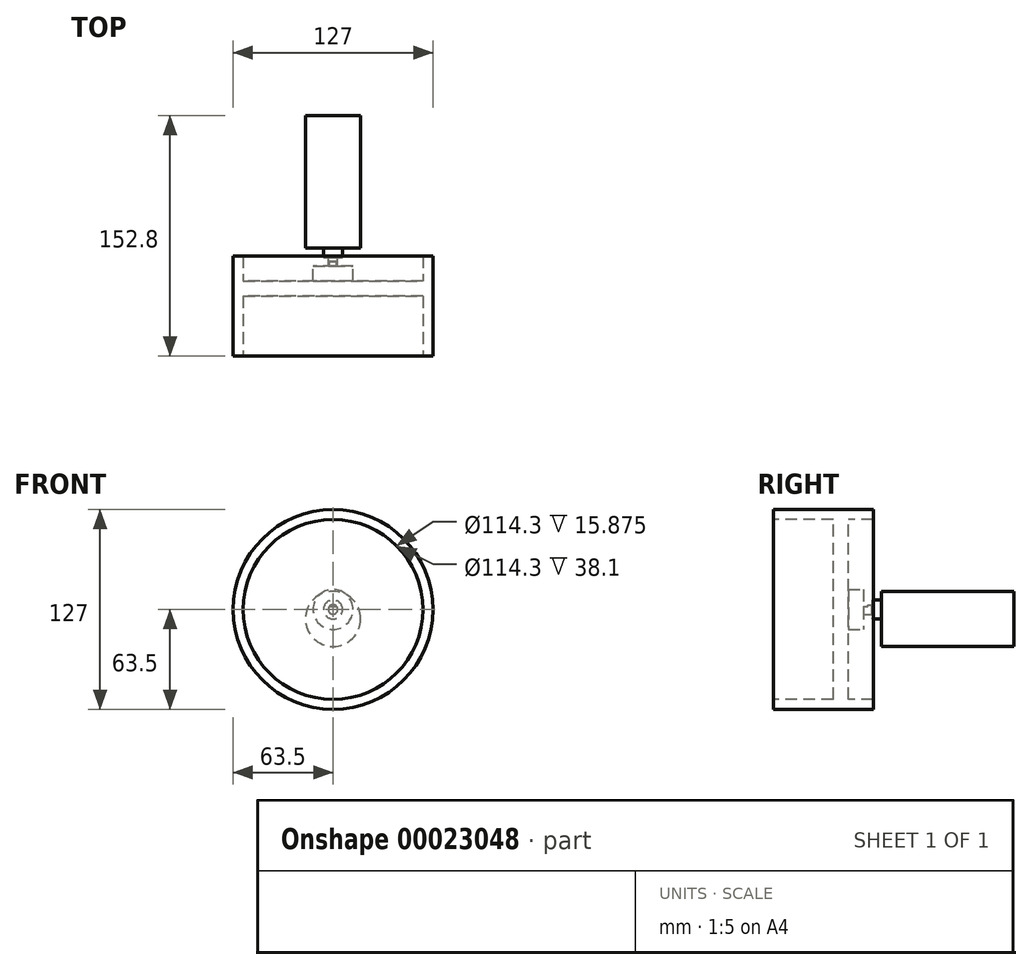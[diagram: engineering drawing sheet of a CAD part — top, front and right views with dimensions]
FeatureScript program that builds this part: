
annotation { "Feature Type Name" : "Feature", "Feature Type Description" : "" }
export const myFeature = defineFeature(function(context is Context, id is Id, definition is map)
    precondition{}
    {
        {
            var Q0;
            Q0=qCreatedBy(makeId("Front.planeOp"),FACE);
            var sketch = newSketch(context, id + "F0", { "sketchPlane" : qUnion([Q0])});
            skArc(sketch, "E0", {"start": v(-2.24, 2) * mm, "mid": v(0, -3) * mm, "end": v(2.24, 2) * mm});
            skPoint(sketch, "E1.start.orphan", {"position": v(0, -3) * mm});
            skPoint(sketch, "E2", {"position": v(-2.24, 2) * mm});
            skPoint(sketch, "E3", {"position": v(2.24, 2) * mm});
            skLineSegment(sketch, "E4", {"start": v(-2.24, 2) * mm, "end": v(2.24, 2) * mm});
            skSolve(sketch);
        }
        {
            var Q0;
            Q0=makeQuery(id+"F0.imprint","IMPRINT",FACE,{"disambiguationData":[TD([[makeQuery(id+"F0.imprint","IMPRINT",EDGE,{"derivedFrom":sQuery(id+"F0.wireOp",EDGE,"E0")}),1.0]])]});
            extrude(context, id + "F1", {"entities" : qUnion([Q0]), "depth" : 22 * mm});
        }
        {
            var Q0;
            Q0=makeQuery(id+"F1.opExtrude","CAP_FACE",FACE,{"disambiguationData":[OSD([sQuery(id+"F0.wireOp",EDGE,"E0"),sQuery(id+"F0.wireOp",EDGE,"E4")])],"isStart":true});
            var sketch = newSketch(context, id + "F2", { "sketchPlane" : qUnion([Q0])});
            skCircle(sketch, "E5", {"center": v(0, 0) * mm, "radius": 3 * mm});
            skSolve(sketch);
        }
        {
            var Q0;
            Q0 = qSketchRegion(id + "F2", true);
            extrude(context, id + "F3", {"entities" : qUnion([Q0]), "operationType" : NewBodyOperationType.ADD, "depth" : 2.5 * mm});
        }
        {
            var Q0;
            Q0=makeQuery(id+"F3.opExtrude","CAP_FACE",FACE,{"disambiguationData":[OSD([sQuery(id+"F2.wireOp",EDGE,"E5")])],"isStart":false});
            var sketch = newSketch(context, id + "F4", { "sketchPlane" : qUnion([Q0])});
            skCircle(sketch, "E6", {"center": v(0, 0) * mm, "radius": 6 * mm});
            skSolve(sketch);
        }
        {
            var Q0;
            Q0 = qSketchRegion(id + "F4", true);
            extrude(context, id + "F5", {"entities" : qUnion([Q0]), "depth" : 6 * mm});
        }
        {
            var Q0;
            Q0=makeQuery(id+"F5.opExtrude","CAP_FACE",FACE,{"disambiguationData":[OSD([sQuery(id+"F4.wireOp",EDGE,"E6")])],"isStart":false});
            var sketch = newSketch(context, id + "F6", { "sketchPlane" : qUnion([Q0])});
            skPoint(sketch, "E7", {"position": v(0, -6) * mm});
            skCircle(sketch, "E8", {"center": v(0, -6) * mm, "radius": 17.5 * mm});
            skSolve(sketch);
        }
        {
            var Q0;
            Q0 = qSketchRegion(id + "F6", true);
            extrude(context, id + "F7", {"entities" : qUnion([Q0]), "operationType" : NewBodyOperationType.ADD, "depth" : 84.2 * mm});
        }
        {
            var Q0;
            Q0=makeQuery(id+"F1.opExtrude","CAP_FACE",FACE,{"disambiguationData":[OSD([sQuery(id+"F0.wireOp",EDGE,"E0"),sQuery(id+"F0.wireOp",EDGE,"E4")])],"isStart":false});
            var sketch = newSketch(context, id + "F8", { "sketchPlane" : qUnion([Q0])});
            skCircle(sketch, "E9", {"center": v(0, 0) * mm, "radius": 63.5 * mm});
            skCircle(sketch, "E10", {"center": v(0, 0) * mm, "radius": 57.15 * mm});
            skSolve(sketch);
        }
        {
            var Q0;
            Q0=makeQuery(id+"F8.imprint","IMPRINT",FACE,{"disambiguationData":[TD([[makeQuery(id+"F8.imprint","IMPRINT",EDGE,{"derivedFrom":sQuery(id+"F8.wireOp",EDGE,"E9")}),1.0]])]});
            extrude(context, id + "F9", {"entities" : qUnion([Q0]), "oppositeDirection" : true, "depth" : 25.4 * mm});
        }
        {
            var Q0;
            Q0=makeQuery(id+"F9.opExtrude","CAP_FACE",FACE,{"disambiguationData":[OSD([sQuery(id+"F8.wireOp",EDGE,"E9"),sQuery(id+"F8.wireOp",EDGE,"E10")])],"isStart":true});
            extrude(context, id + "F10", {"entities" : qUnion([Q0]), "operationType" : NewBodyOperationType.ADD, "depth" : 38.1 * mm});
        }
        {
            var Q0;
            Q0=makeQuery(id+"F1.opExtrude","CAP_FACE",FACE,{"disambiguationData":[OSD([sQuery(id+"F0.wireOp",EDGE,"E0"),sQuery(id+"F0.wireOp",EDGE,"E4")])],"isStart":false});
            var sketch = newSketch(context, id + "F11", { "sketchPlane" : qUnion([Q0])});
            skCircle(sketch, "E11", {"center": v(0, 0) * mm, "radius": 57.15 * mm});
            skSolve(sketch);
        }
        {
            var Q0;
            Q0=makeQuery(id+"F11.imprint","IMPRINT",FACE,{"disambiguationData":[TD([[makeQuery(id+"F11.imprint","IMPRINT",EDGE,{"derivedFrom":sQuery(id+"F11.wireOp",EDGE,"E11")}),1.0]])]});
            extrude(context, id + "F12", {"entities" : qUnion([Q0]), "operationType" : NewBodyOperationType.ADD, "oppositeDirection" : true, "depth" : 19.05 * mm});
        }
        {
            var Q0;
            Q0=makeQuery(id+"F12.opExtrude","CAP_FACE",FACE,{"disambiguationData":[OSD([sQuery(id+"F0.wireOp",EDGE,"E0"),sQuery(id+"F0.wireOp",EDGE,"E4"),sQuery(id+"F11.wireOp",EDGE,"E11")])],"isStart":false});
            var sketch = newSketch(context, id + "F13", { "sketchPlane" : qUnion([Q0])});
            skCircle(sketch, "E12", {"center": v(0, 0) * mm, "radius": 12.7 * mm});
            skCircle(sketch, "E13", {"center": v(0, 0) * mm, "radius": 57.15 * mm});
            skSolve(sketch);
        }
        {
            var Q0;
            Q0 = qSketchRegion(id + "F13", true);
            extrude(context, id + "F14", {"entities" : qUnion([Q0]), "operationType" : NewBodyOperationType.REMOVE, "oppositeDirection" : true, "depth" : 9.52 * mm});
        }
    });
